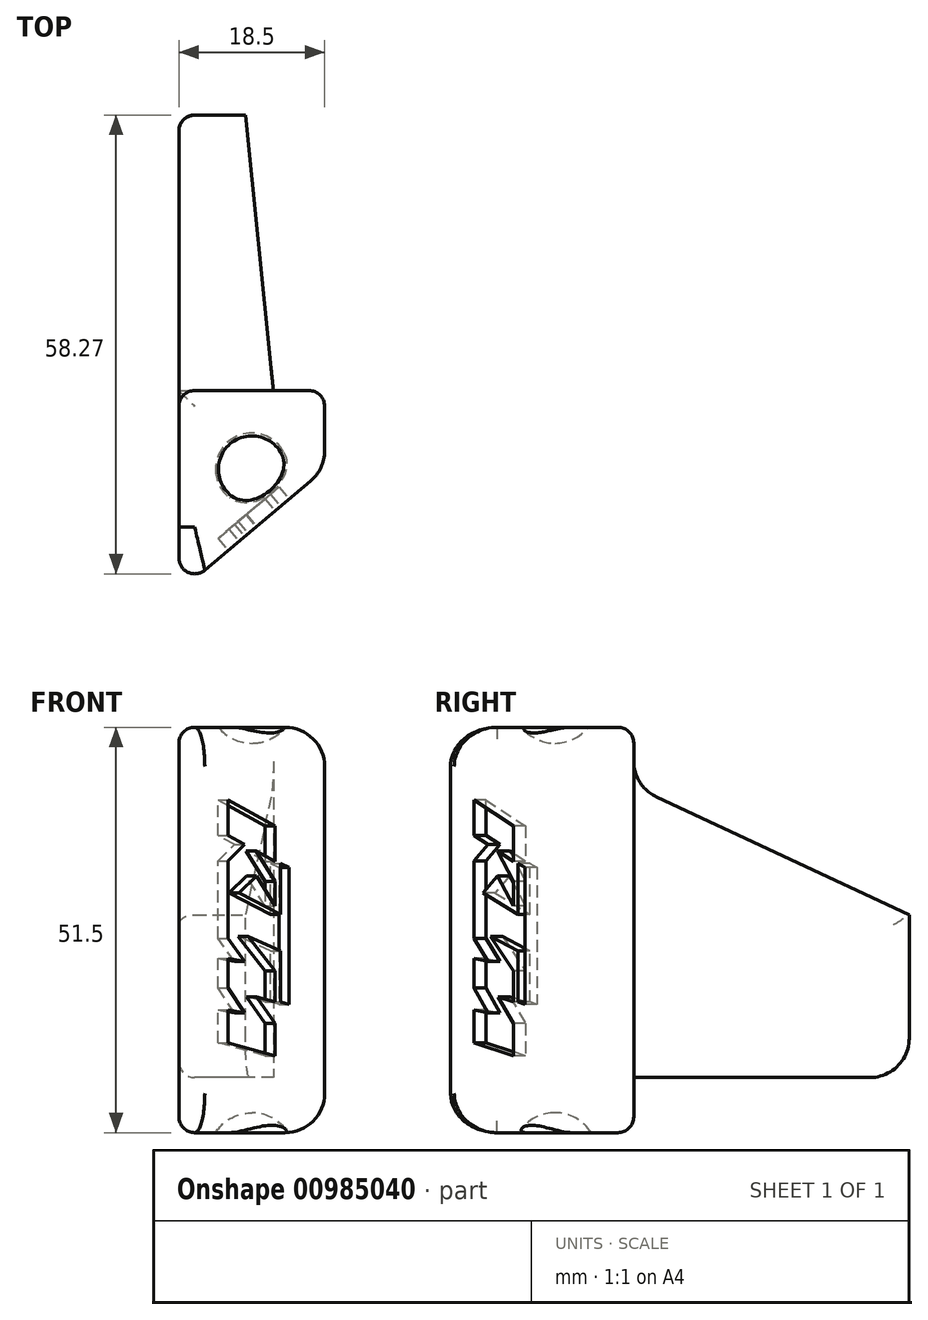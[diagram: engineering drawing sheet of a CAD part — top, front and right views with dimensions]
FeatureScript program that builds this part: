
annotation { "Feature Type Name" : "Feature", "Feature Type Description" : "" }
export const myFeature = defineFeature(function(context is Context, id is Id, definition is map)
    precondition{}
    {
        {
            var Q0;
            Q0=qCreatedBy(makeId("Front.planeOp"),FACE);
            var sketch = newSketch(context, id + "F0", { "sketchPlane" : qUnion([Q0])});
            skLineSegment(sketch, "E0.bottom", {"start": v(-6, 25.5) * mm, "end": v(12.5, 25.5) * mm});
            skLineSegment(sketch, "E0.top", {"start": v(-6, -26) * mm, "end": v(12.5, -26) * mm});
            skLineSegment(sketch, "E0.left", {"start": v(-6, 25.5) * mm, "end": v(-6, -26) * mm});
            skLineSegment(sketch, "E0.right", {"start": v(12.5, 25.5) * mm, "end": v(12.5, -26) * mm});
            skSolve(sketch);
        }
        {
            var Q0;
            Q0 = qSketchRegion(id + "F0", true);
            extrude(context, id + "F1", {"entities" : qUnion([Q0]), "oppositeDirection" : true, "depth" : 5 * mm, "offsetDistance" : 25 * mm});
        }
        {
            var Q0;
            Q0=makeQuery(id+"F1.opExtrude","CAP_FACE",FACE,{"disambiguationData":[OSD([sQuery(id+"F0.wireOp",EDGE,"E0.bottom"),sQuery(id+"F0.wireOp",EDGE,"E0.top"),sQuery(id+"F0.wireOp",EDGE,"E0.left"),sQuery(id+"F0.wireOp",EDGE,"E0.right")])],"isStart":false});
            var sketch = newSketch(context, id + "F2", { "sketchPlane" : qUnion([Q0])});
            skLineSegment(sketch, "E1.bottom", {"start": v(-6, 18) * mm, "end": v(6, 18) * mm});
            skLineSegment(sketch, "E1.top", {"start": v(-6, -19) * mm, "end": v(6, -19) * mm});
            skLineSegment(sketch, "E1.left", {"start": v(-6, 18) * mm, "end": v(-6, -19) * mm});
            skLineSegment(sketch, "E1.right", {"start": v(6, 18) * mm, "end": v(6, -19) * mm});
            skSolve(sketch);
        }
        {
            var Q0;
            Q0 = qSketchRegion(id + "F2", true);
            extrude(context, id + "F3", {"entities" : qUnion([Q0]), "operationType" : NewBodyOperationType.ADD, "depth" : 35 * mm, "offsetDistance" : 25 * mm});
        }
        {
            var Q0;
            Q0=makeQuery(id+"F3.opExtrude","SWEPT_FACE",FACE,{"disambiguationData":[OSD([sQuery(id+"F2.wireOp",EDGE,"E1.left")])]});
            var sketch = newSketch(context, id + "F4", { "sketchPlane" : qUnion([Q0])});
            skLineSegment(sketch, "E2", {"start": v(5, 18) * mm, "end": v(40, 1.68) * mm});
            skLineSegment(sketch, "E3", {"start": v(40, 1.68) * mm, "end": v(40, 18) * mm});
            skLineSegment(sketch, "E4", {"start": v(40, 18) * mm, "end": v(5, 18) * mm});
            skSolve(sketch);
        }
        {
            var Q0;
            Q0=makeQuery(id+"F3.opExtrude","SWEPT_FACE",FACE,{"disambiguationData":[OSD([sQuery(id+"F2.wireOp",EDGE,"E1.bottom")])]});
            var sketch = newSketch(context, id + "F5", { "sketchPlane" : qUnion([Q0])});
            skLineSegment(sketch, "E5", {"start": v(6, 5) * mm, "end": v(2.44, 40) * mm});
            skLineSegment(sketch, "E6", {"start": v(2.44, 40) * mm, "end": v(6, 40) * mm});
            skLineSegment(sketch, "E7", {"start": v(6, 40) * mm, "end": v(6, 5) * mm});
            skSolve(sketch);
        }
        {
            var Q0;
            Q0=qCreatedBy(makeId("Front.planeOp"),FACE);
            cPlane(context, id + "F6", {"entities" : qUnion([Q0]), "cplaneType" : CPlaneType.OFFSET, "offset" : 5 * mm, "width" : 150 * mm, "height" : 150 * mm});
        }
        {
            var Q0;
            Q0=qCreatedBy(makeId("Top.planeOp"),FACE);
            var sketch = newSketch(context, id + "F7", { "sketchPlane" : qUnion([Q0])});
            skLineSegment(sketch, "E8", {"start": v(12.5, -5) * mm, "end": v(-6, -20.57) * mm});
            skLineSegment(sketch, "E9", {"start": v(-6, -20.57) * mm, "end": v(-6, 0) * mm});
            skLineSegment(sketch, "E10", {"start": v(12.5, -5) * mm, "end": v(12.5, 0) * mm});
            skLineSegment(sketch, "E11", {"start": v(12.5, 0) * mm, "end": v(-6, 0) * mm});
            skSolve(sketch);
        }
        {
            var Q0;
            Q0 = qSketchRegion(id + "F5", true);
            extrude(context, id + "F8", {"entities" : qUnion([Q0]), "operationType" : NewBodyOperationType.REMOVE, "endBound" : BoundingType.SYMMETRIC, "oppositeDirection" : true, "depth" : 100 * mm, "offsetDistance" : 25 * mm});
        }
        {
            var Q0;
            Q0 = qSketchRegion(id + "F4", true);
            extrude(context, id + "F9", {"entities" : qUnion([Q0]), "operationType" : NewBodyOperationType.REMOVE, "endBound" : BoundingType.SYMMETRIC, "oppositeDirection" : true, "depth" : 25 * mm, "offsetDistance" : 25 * mm});
        }
        {
            var Q0;
            Q0=makeQuery(id+"F7.imprint","IMPRINT",FACE,{"disambiguationData":[TD([[makeQuery(id+"F7.imprint","IMPRINT",EDGE,{"derivedFrom":sQuery(id+"F7.wireOp",EDGE,"E8")}),-1.0]])]});
            extrude(context, id + "F10", {"entities" : qUnion([Q0]), "operationType" : NewBodyOperationType.ADD, "depth" : 25.5 * mm, "offsetDistance" : 25 * mm, "hasSecondDirection" : true, "secondDirectionOppositeDirection" : true, "secondDirectionDepth" : 26 * mm});
        }
        {
            var Q0;
            Q0=makeQuery(id+"F9.boolean.opBoolean","MERGE",EDGE,{"derivedFrom":[makeQuery(id+"F3.opExtrude","CAP_EDGE",EDGE,{"disambiguationData":[OSD([sQuery(id+"F2.wireOp",EDGE,"E1.bottom")])],"isStart":true})],"fromTools":[makeQuery(id+"F9.opExtrude","SWEPT_EDGE",EDGE,{"disambiguationData":[OSD([sQuery(id+"F2.wireOp",EDGE,"E1.left"),sQuery(id+"F4.wireOp",EDGE,"E2"),sQuery(id+"F4.wireOp",EDGE,"E4")])]})]});
            var Q1;
            Q1=makeQuery(id+"F3.opExtrude","CAP_EDGE",EDGE,{"disambiguationData":[OSD([sQuery(id+"F2.wireOp",EDGE,"E1.top")])],"isStart":true});
            var Q2;
            Q2=makeQuery(id+"F9.boolean.opBoolean","COPY",EDGE,{"derivedFrom":makeQuery(id+"F9.opExtrude","SWEPT_EDGE",EDGE,{"disambiguationData":[OSD([sQuery(id+"F2.wireOp",EDGE,"E1.left"),sQuery(id+"F4.wireOp",EDGE,"E2"),sQuery(id+"F4.wireOp",EDGE,"E3")])]})});
            var Q3;
            Q3=makeQuery(id+"F3.opExtrude","CAP_EDGE",EDGE,{"disambiguationData":[OSD([sQuery(id+"F2.wireOp",EDGE,"E1.top")])],"isStart":false});
            var Q4;
            Q4=makeQuery(id+"F3.opExtrude","CAP_EDGE",EDGE,{"disambiguationData":[OSD([sQuery(id+"F2.wireOp",EDGE,"E1.left")])],"isStart":false});
            var Q5;
            Q5=makeQuery(id+"F10.boolean.opBoolean","MERGE",EDGE,{"derivedFrom":[makeQuery(id+"F1.opExtrude","CAP_EDGE",EDGE,{"disambiguationData":[OSD([sQuery(id+"F0.wireOp",EDGE,"E0.right")])],"isStart":true}),makeQuery(id+"F10.opExtrude","SWEPT_EDGE",EDGE,{"disambiguationData":[OSD([sQuery(id+"F7.wireOp",EDGE,"E8"),sQuery(id+"F7.wireOp",EDGE,"j6gPKiCe-Spyz-P0aa-3LFO-MI6PPOXaBDCZ")])]})]});
            var Q6;
            Q6=makeQuery(id+"F10.opExtrude","CAP_EDGE",EDGE,{"disambiguationData":[OSD([sQuery(id+"F7.wireOp",EDGE,"E8")])],"isStart":false});
            var Q7;
            Q7=makeQuery(id+"F10.opExtrude","CAP_EDGE",EDGE,{"disambiguationData":[OSD([sQuery(id+"F7.wireOp",EDGE,"E8")])],"isStart":true});
            var Q8;
            Q8=makeQuery(id+"F10.opExtrude","SWEPT_EDGE",EDGE,{"disambiguationData":[OSD([sQuery(id+"F7.wireOp",EDGE,"E8"),sQuery(id+"F7.wireOp",EDGE,"E10")])]});
            var Q9;
            Q9=makeQuery(id+"F10.boolean.opBoolean","MERGE",EDGE,{"derivedFrom":[makeQuery(id+"F1.opExtrude","SWEPT_EDGE",EDGE,{"disambiguationData":[OSD([sQuery(id+"F0.wireOp",EDGE,"E0.bottom"),sQuery(id+"F0.wireOp",EDGE,"E0.right")])]}),makeQuery(id+"F10.opExtrude","CAP_EDGE",EDGE,{"disambiguationData":[OSD([sQuery(id+"F7.wireOp",EDGE,"E10")])],"isStart":false})]});
            var Q10;
            Q10=makeQuery(id+"F10.boolean.opBoolean","MERGE",EDGE,{"derivedFrom":[makeQuery(id+"F1.opExtrude","SWEPT_EDGE",EDGE,{"disambiguationData":[OSD([sQuery(id+"F0.wireOp",EDGE,"E0.top"),sQuery(id+"F0.wireOp",EDGE,"E0.right")])]}),makeQuery(id+"F10.opExtrude","CAP_EDGE",EDGE,{"disambiguationData":[OSD([sQuery(id+"F7.wireOp",EDGE,"E10")])],"isStart":true})]});
            fillet(context, id + "F11", {"entities" : qUnion([Q0, Q1, Q2, Q3, Q4, Q5, Q6, Q7, Q8, Q9, Q10]), "radius" : 5 * mm, "tangentPropagation" : true, "allowEdgeOverflow" : false});
        }
        {
            var Q0;
            Q0=makeQuery(id+"F9.boolean.opBoolean","INTERSECT",EDGE,{"derivedFrom":[makeQuery(id+"F3.opExtrude","SWEPT_FACE",FACE,{"disambiguationData":[OSD([sQuery(id+"F2.wireOp",EDGE,"E1.left")])]}),makeQuery(id+"F9.opExtrude","SWEPT_FACE",FACE,{"disambiguationData":[OSD([sQuery(id+"F4.wireOp",EDGE,"E2")])]})]});
            var Q1;
            Q1=makeQuery(id+"F9.boolean.opBoolean","INTERSECT",EDGE,{"derivedFrom":[makeQuery(id+"F3.opExtrude","SWEPT_FACE",FACE,{"disambiguationData":[OSD([sQuery(id+"F2.wireOp",EDGE,"E1.right")])]}),makeQuery(id+"F9.opExtrude","SWEPT_FACE",FACE,{"disambiguationData":[OSD([sQuery(id+"F4.wireOp",EDGE,"E2")])]})]});
            var Q2;
            Q2=makeQuery(id+"F3.opExtrude","SWEPT_EDGE",EDGE,{"disambiguationData":[OSD([sQuery(id+"F2.wireOp",EDGE,"E1.top"),sQuery(id+"F2.wireOp",EDGE,"E1.left")])]});
            var Q3;
            Q3=makeQuery(id+"F3.opExtrude","SWEPT_EDGE",EDGE,{"disambiguationData":[OSD([sQuery(id+"F2.wireOp",EDGE,"E1.top"),sQuery(id+"F2.wireOp",EDGE,"E1.right")])]});
            var Q4;
            Q4=makeQuery(id+"F1.opExtrude","CAP_EDGE",EDGE,{"disambiguationData":[OSD([sQuery(id+"F0.wireOp",EDGE,"E0.bottom")])],"isStart":false});
            var Q5;
            Q5=makeQuery(id+"F1.opExtrude","SWEPT_EDGE",EDGE,{"disambiguationData":[OSD([sQuery(id+"F0.wireOp",EDGE,"E0.bottom"),sQuery(id+"F0.wireOp",EDGE,"E0.left")])]});
            var Q6;
            Q6=makeQuery(id+"F1.opExtrude","SWEPT_EDGE",EDGE,{"disambiguationData":[OSD([sQuery(id+"F0.wireOp",EDGE,"E0.top"),sQuery(id+"F0.wireOp",EDGE,"E0.left")])]});
            var Q7;
            Q7=makeQuery(id+"F1.opExtrude","CAP_EDGE",EDGE,{"disambiguationData":[OSD([sQuery(id+"F0.wireOp",EDGE,"E0.top")])],"isStart":false});
            fillet(context, id + "F12", {"entities" : qUnion([Q0, Q1, Q2, Q3, Q4, Q5, Q6, Q7]), "radius" : 2 * mm, "tangentPropagation" : true, "allowEdgeOverflow" : false});
        }
        {
            var Q0;
            Q0=makeQuery(id+"F10.opExtrude","SWEPT_FACE",FACE,{"disambiguationData":[OSD([sQuery(id+"F7.wireOp",EDGE,"E8")])]});
            var sketch = newSketch(context, id + "F13", { "sketchPlane" : qUnion([Q0])});
            skLineSegment(sketch, "E12.0", {"start": v(-9.67, 16.28) * mm, "end": v(-1.87, 12.96) * mm});
            skLineSegment(sketch, "E12.1", {"start": v(-1.87, 8.46) * mm, "end": v(-5.02, 9.8) * mm});
            skLineSegment(sketch, "E12.2", {"start": v(-9.67, 11.78) * mm, "end": v(-9.67, 16.28) * mm});
            skLineSegment(sketch, "E12.3", {"start": v(-6.92, 10.6) * mm, "end": v(-9.67, 11.78) * mm});
            skLineSegment(sketch, "E12.4", {"start": v(-9.67, 8.53) * mm, "end": v(-6.92, 10.6) * mm});
            skLineSegment(sketch, "E12.5", {"start": v(-5.02, 9.8) * mm, "end": v(-1.87, 5.91) * mm});
            skLineSegment(sketch, "E12.6", {"start": v(-1.87, 2.81) * mm, "end": v(-4.97, 6.64) * mm});
            skLineSegment(sketch, "E12.7", {"start": v(-9.67, -1.32) * mm, "end": v(-9.67, 8.53) * mm});
            skLineSegment(sketch, "E12.8", {"start": v(-4.97, 6.64) * mm, "end": v(-7.87, 4.45) * mm});
            skLineSegment(sketch, "E12.9", {"start": v(0.43, 7.68) * mm, "end": v(0.43, -9.71) * mm});
            skLineSegment(sketch, "E12.10", {"start": v(-0.97, 8.19) * mm, "end": v(0.43, 7.68) * mm});
            skLineSegment(sketch, "E12.11", {"start": v(-0.97, 1.74) * mm, "end": v(-0.97, 8.19) * mm});
            skLineSegment(sketch, "E12.12", {"start": v(-7.87, 4.45) * mm, "end": v(-0.97, 1.74) * mm});
            skLineSegment(sketch, "E12.13", {"start": v(-1.87, 5.91) * mm, "end": v(-1.87, 2.81) * mm});
            skLineSegment(sketch, "E12.14", {"start": v(-1.87, 12.96) * mm, "end": v(-1.87, 8.46) * mm});
            skLineSegment(sketch, "E12.15", {"start": v(-0.97, -2.91) * mm, "end": v(-6.37, -1.05) * mm});
            skLineSegment(sketch, "E12.16", {"start": v(-0.97, -9.41) * mm, "end": v(-0.97, -2.91) * mm});
            skLineSegment(sketch, "E12.17", {"start": v(0.43, -9.71) * mm, "end": v(-0.97, -9.41) * mm});
            skLineSegment(sketch, "E12.18", {"start": v(-6.37, -1.05) * mm, "end": v(-1.87, -5.48) * mm});
            skLineSegment(sketch, "E12.19", {"start": v(-1.87, -5.48) * mm, "end": v(-1.87, -9.38) * mm});
            skLineSegment(sketch, "E12.20", {"start": v(-1.87, -9.38) * mm, "end": v(-4.92, -8.73) * mm});
            skLineSegment(sketch, "E12.21", {"start": v(-4.92, -8.73) * mm, "end": v(-1.87, -12.11) * mm});
            skLineSegment(sketch, "E12.22", {"start": v(-1.87, -12.11) * mm, "end": v(-1.87, -16.22) * mm});
            skLineSegment(sketch, "E12.23", {"start": v(-1.87, -16.22) * mm, "end": v(-9.67, -14.56) * mm});
            skLineSegment(sketch, "E12.24", {"start": v(-9.67, -14.56) * mm, "end": v(-9.67, -10.41) * mm});
            skLineSegment(sketch, "E12.25", {"start": v(-9.67, -10.41) * mm, "end": v(-6.92, -10.8) * mm});
            skLineSegment(sketch, "E12.26", {"start": v(-6.92, -10.8) * mm, "end": v(-9.67, -7.64) * mm});
            skLineSegment(sketch, "E12.27", {"start": v(-9.67, -7.64) * mm, "end": v(-9.67, -3.89) * mm});
            skLineSegment(sketch, "E12.28", {"start": v(-9.67, -3.89) * mm, "end": v(-6.92, -4.27) * mm});
            skLineSegment(sketch, "E12.29", {"start": v(-6.92, -4.27) * mm, "end": v(-9.67, -1.32) * mm});
            skSolve(sketch);
        }
        {
            var Q0;
            Q0 = qSketchRegion(id + "F13", true);
            extrude(context, id + "F14", {"entities" : qUnion([Q0]), "operationType" : NewBodyOperationType.REMOVE, "oppositeDirection" : true, "depth" : 2 * mm, "offsetDistance" : 25 * mm});
        }
        {
            var Q0;
            Q0=qCreatedBy(id+"F6.planeOp",FACE);
            var sketch = newSketch(context, id + "F15", { "sketchPlane" : qUnion([Q0])});
            skArc(sketch, "E13", {"start": v(3.26, 34.4) * mm, "mid": v(-2.2, 28.93) * mm, "end": v(3.26, 23.47) * mm});
            skLineSegment(sketch, "E14", {"start": v(3.26, 22.32) * mm, "end": v(3.26, 42.34) * mm, "construction": true});
            skLineSegment(sketch, "E15", {"start": v(3.26, 23.47) * mm, "end": v(3.26, 34.4) * mm});
            skArc(sketch, "E16.MirrorCS", {"start": v(3.26, -34.4) * mm, "mid": v(-2.2, -28.93) * mm, "end": v(3.26, -23.47) * mm});
            skLineSegment(sketch, "E17.MirrorCS", {"start": v(3.26, -22.32) * mm, "end": v(3.26, -42.34) * mm, "construction": true});
            skLineSegment(sketch, "E18", {"start": v(3.26, -23.47) * mm, "end": v(3.26, -34.4) * mm});
            skSolve(sketch);
        }
        {
            var Q0;
            Q0 = qSketchRegion(id + "F15", true);
            var Q1;
            Q1=sQuery(id+"F15.wireOp",EDGE,"E14");
            revolve(context, id + "F16", {"operationType" : NewBodyOperationType.REMOVE, "surfaceOperationType" : NewSurfaceOperationType.NEW, "entities" : qUnion([Q0]), "axis" : qUnion([Q1]), "revolveType" : RevolveType.FULL, "oppositeDirection" : true});
        }
    });
